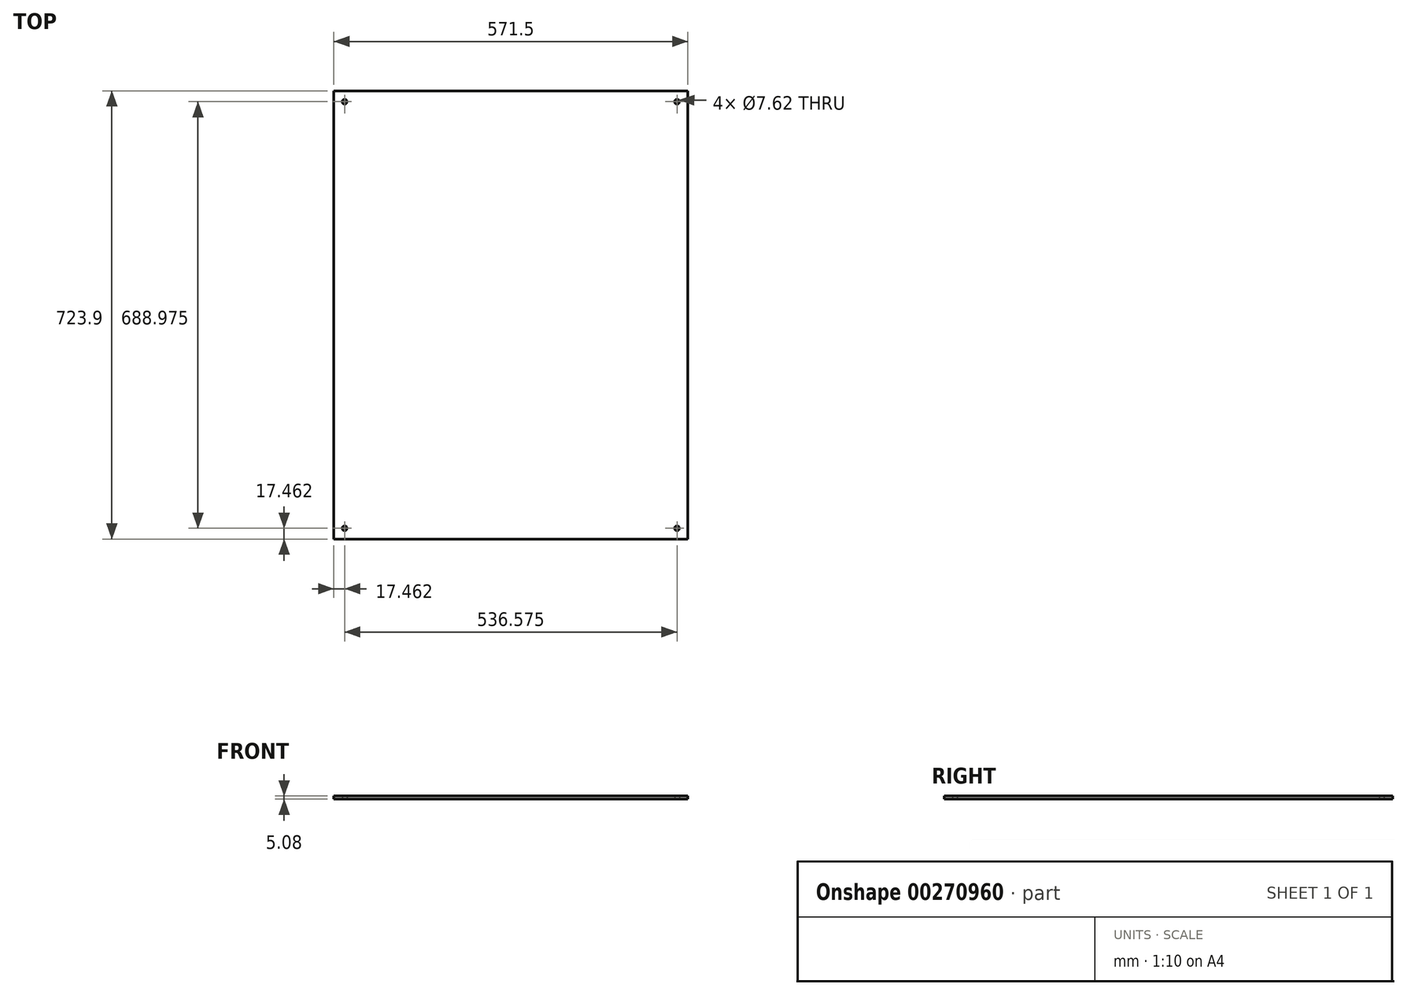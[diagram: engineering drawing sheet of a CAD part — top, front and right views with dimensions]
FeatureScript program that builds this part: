
annotation { "Feature Type Name" : "Feature", "Feature Type Description" : "" }
export const myFeature = defineFeature(function(context is Context, id is Id, definition is map)
    precondition{}
    {
        {
            var Q0;
            Q0=qCreatedBy(makeId("Top.planeOp"),FACE);
            var sketch = newSketch(context, id + "F0", { "sketchPlane" : qUnion([Q0])});
            skLineSegment(sketch, "E0.bottom", {"start": v(-285.75, 361.95) * mm, "end": v(285.75, 361.95) * mm});
            skLineSegment(sketch, "E0.top", {"start": v(-285.75, -361.95) * mm, "end": v(285.75, -361.95) * mm});
            skLineSegment(sketch, "E0.left", {"start": v(-285.75, 361.95) * mm, "end": v(-285.75, -361.95) * mm});
            skLineSegment(sketch, "E0.right", {"start": v(285.75, 361.95) * mm, "end": v(285.75, -361.95) * mm});
            skPoint(sketch, "E0.middle", {"position": v(0, 0) * mm});
            skLineSegment(sketch, "E1", {"start": v(0, -361.95) * mm, "end": v(0, 361.95) * mm, "construction": true});
            skLineSegment(sketch, "E2", {"start": v(-285.75, 0) * mm, "end": v(285.75, 0) * mm, "construction": true});
            skPoint(sketch, "E3", {"position": v(-268.29, 344.49) * mm});
            skPoint(sketch, "E4.MirrorP", {"position": v(268.29, 344.49) * mm});
            skPoint(sketch, "E5.MirrorP", {"position": v(-268.29, -344.49) * mm});
            skPoint(sketch, "E6.MirrorP", {"position": v(268.29, -344.49) * mm});
            skCircle(sketch, "E7", {"center": v(-268.29, 344.49) * mm, "radius": 3.81 * mm});
            skCircle(sketch, "E8", {"center": v(268.29, 344.49) * mm, "radius": 3.81 * mm});
            skCircle(sketch, "E9", {"center": v(-268.29, -344.49) * mm, "radius": 3.81 * mm});
            skCircle(sketch, "E10", {"center": v(268.29, -344.49) * mm, "radius": 3.81 * mm});
            skSolve(sketch);
        }
        {
            var Q0;
            Q0=makeQuery(id+"F0.imprint","IMPRINT",FACE,{"disambiguationData":[TD([[makeQuery(id+"F0.imprint","IMPRINT",EDGE,{"derivedFrom":sQuery(id+"F0.wireOp",EDGE,"E0.bottom")}),-1.0]])]});
            extrude(context, id + "F1", {"entities" : qUnion([Q0]), "depth" : 5.08 * mm});
        }
    });
